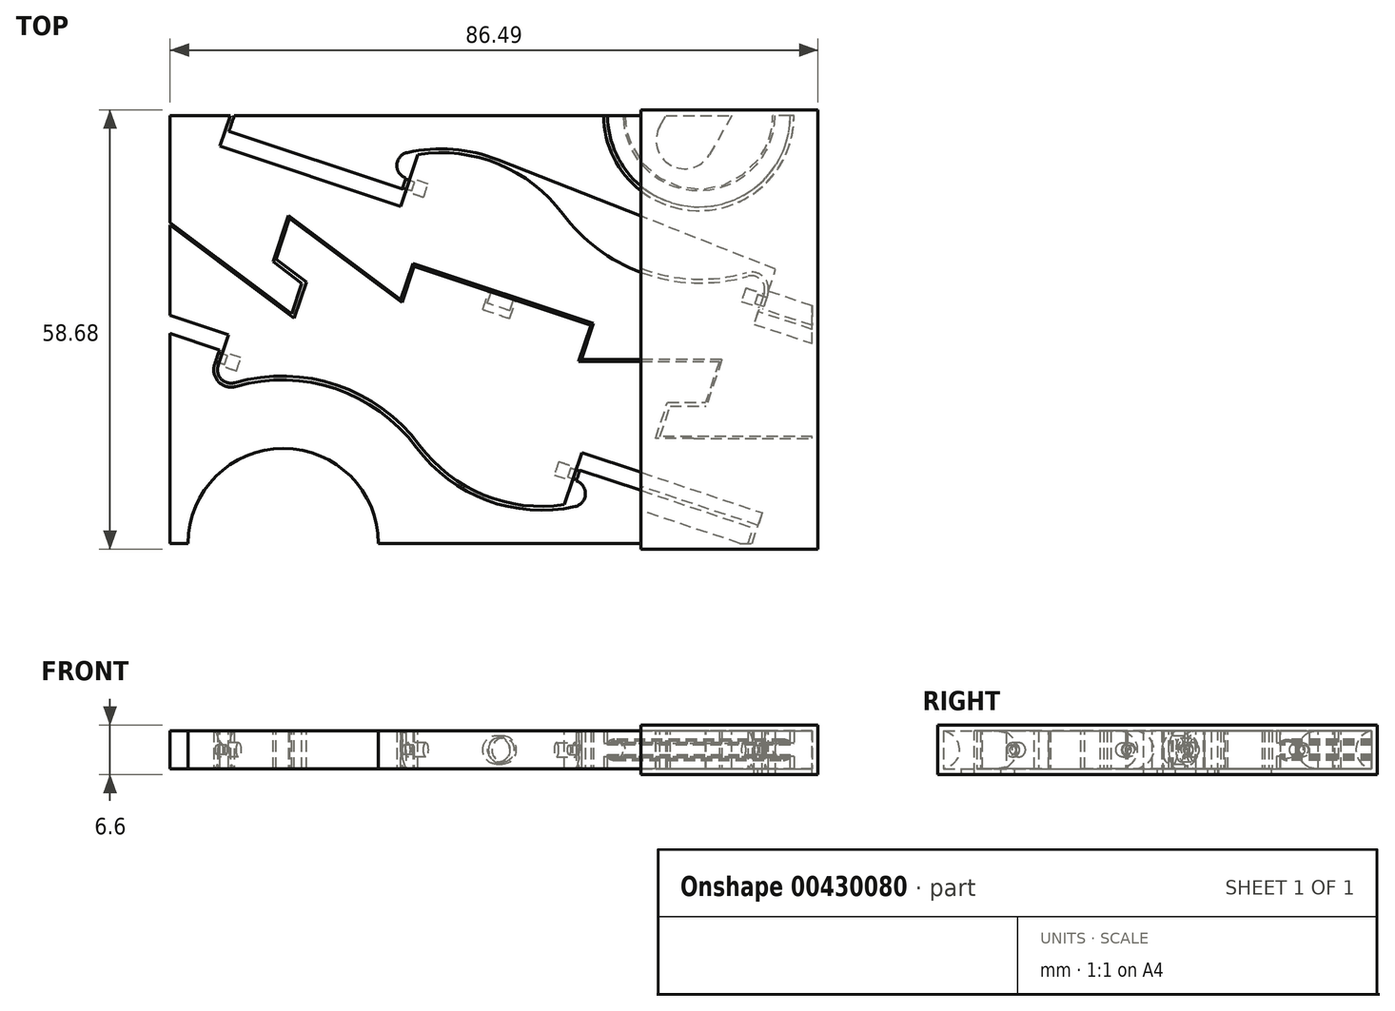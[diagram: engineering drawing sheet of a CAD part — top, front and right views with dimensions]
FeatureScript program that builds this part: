
annotation { "Feature Type Name" : "Feature", "Feature Type Description" : "" }
export const myFeature = defineFeature(function(context is Context, id is Id, definition is map)
    precondition{}
    {
        {
            var Q0;
            Q0=qCreatedBy(makeId("Top.planeOp"),FACE);
            cPlane(context, id + "F0", {"entities" : qUnion([Q0]), "cplaneType" : CPlaneType.OFFSET, "offset" : 2.54 * mm, "width" : 152.4 * mm, "height" : 152.4 * mm});
        }
        {
            var Q0;
            Q0=qCreatedBy(makeId("Top.planeOp"),FACE);
            var sketch = newSketch(context, id + "F1", { "sketchPlane" : qUnion([Q0])});
            skLineSegment(sketch, "E0", {"start": v(0, 0) * mm, "end": v(0, 28.58) * mm});
            skLineSegment(sketch, "E1", {"start": v(0, 0) * mm, "end": v(85.73, 0) * mm, "construction": true});
            skLineSegment(sketch, "E2", {"start": v(0, 28.58) * mm, "end": v(85.73, 0) * mm, "construction": true});
            skLineSegment(sketch, "E3", {"start": v(0, 28.58) * mm, "end": v(8.03, 28.58) * mm});
            skLineSegment(sketch, "E4", {"start": v(8.03, 28.58) * mm, "end": v(7.23, 26.17) * mm});
            skLineSegment(sketch, "E5", {"start": v(7.23, 26.17) * mm, "end": v(31.33, 18.13) * mm});
            skLineSegment(sketch, "E6", {"start": v(31.33, 18.13) * mm, "end": v(32.13, 20.54) * mm});
            skLineSegment(sketch, "E7", {"start": v(32.13, 20.54) * mm, "end": v(31.65, 20.7) * mm});
            skArc(sketch, "E8", {"start": v(31.78, 23.15) * mm, "mid": v(30.78, 21.98) * mm, "end": v(31.65, 20.7) * mm});
            skArc(sketch, "E9", {"start": v(52.44, 15.43) * mm, "mid": v(43.25, 22.34) * mm, "end": v(31.78, 23.15) * mm});
            skArc(sketch, "E10", {"start": v(52.44, 15.43) * mm, "mid": v(63.47, 7.42) * mm, "end": v(77.1, 7.11) * mm});
            skArc(sketch, "E11", {"start": v(79.3, 4.82) * mm, "mid": v(78.9, 6.63) * mm, "end": v(77.1, 7.11) * mm});
            skLineSegment(sketch, "E12", {"start": v(79.3, 4.82) * mm, "end": v(78.5, 2.4) * mm});
            skLineSegment(sketch, "E13", {"start": v(78.5, 2.4) * mm, "end": v(85.73, 0) * mm});
            skLineSegment(sketch, "E14", {"start": v(0, 0) * mm, "end": v(0, -28.58) * mm, "construction": true});
            skLineSegment(sketch, "E15", {"start": v(0, -28.58) * mm, "end": v(85.73, -28.58) * mm, "construction": true});
            skLineSegment(sketch, "E16", {"start": v(0, 14.29) * mm, "end": v(85.73, -14.29) * mm, "construction": true});
            skLineSegment(sketch, "E17", {"start": v(85.73, 0) * mm, "end": v(85.73, -14.29) * mm});
            skLineSegment(sketch, "E18", {"start": v(85.73, -14.29) * mm, "end": v(70.23, -14.29) * mm});
            skLineSegment(sketch, "E19", {"start": v(73.65, -4.02) * mm, "end": v(54.91, -4.02) * mm});
            skLineSegment(sketch, "E20", {"start": v(54.91, -4.02) * mm, "end": v(56.52, 0.8) * mm});
            skLineSegment(sketch, "E21", {"start": v(56.52, 0.8) * mm, "end": v(32.42, 8.84) * mm});
            skLineSegment(sketch, "E22", {"start": v(32.42, 8.84) * mm, "end": v(30.81, 4.02) * mm});
            skLineSegment(sketch, "E23", {"start": v(30.81, 4.02) * mm, "end": v(15.82, 15.26) * mm});
            skLineSegment(sketch, "E24", {"start": v(12.4, 5) * mm, "end": v(0, 14.29) * mm});
            skLineSegment(sketch, "E25", {"start": v(15.82, 15.26) * mm, "end": v(12.4, 5) * mm});
            skLineSegment(sketch, "E26", {"start": v(73.65, -4.02) * mm, "end": v(70.23, -14.29) * mm});
            skSolve(sketch);
        }
        {
            var Q0;
            Q0=qCreatedBy(makeId("Top.planeOp"),FACE);
            var sketch = newSketch(context, id + "F2", { "sketchPlane" : qUnion([Q0])});
            skLineSegment(sketch, "E27", {"start": v(85.73, 0) * mm, "end": v(85.73, -28.58) * mm, "construction": true});
            skLineSegment(sketch, "E28", {"start": v(85.73, 0) * mm, "end": v(0, 0) * mm, "construction": true});
            skLineSegment(sketch, "E29", {"start": v(85.73, -28.58) * mm, "end": v(0, 0) * mm, "construction": true});
            skLineSegment(sketch, "E30", {"start": v(85.73, -28.58) * mm, "end": v(77.7, -28.58) * mm});
            skLineSegment(sketch, "E31", {"start": v(77.7, -28.58) * mm, "end": v(78.5, -26.17) * mm});
            skLineSegment(sketch, "E32", {"start": v(78.5, -26.17) * mm, "end": v(54.4, -18.13) * mm});
            skLineSegment(sketch, "E33", {"start": v(54.4, -18.13) * mm, "end": v(53.6, -20.54) * mm});
            skLineSegment(sketch, "E34", {"start": v(53.6, -20.54) * mm, "end": v(54.08, -20.7) * mm});
            skArc(sketch, "E35", {"start": v(53.95, -23.15) * mm, "mid": v(54.94, -21.98) * mm, "end": v(54.08, -20.7) * mm});
            skArc(sketch, "E36", {"start": v(33.29, -15.43) * mm, "mid": v(42.48, -22.34) * mm, "end": v(53.95, -23.15) * mm});
            skArc(sketch, "E37", {"start": v(33.29, -15.43) * mm, "mid": v(22.26, -7.42) * mm, "end": v(8.62, -7.11) * mm});
            skArc(sketch, "E38", {"start": v(6.43, -4.82) * mm, "mid": v(6.83, -6.63) * mm, "end": v(8.62, -7.11) * mm});
            skLineSegment(sketch, "E39", {"start": v(6.43, -4.82) * mm, "end": v(7.23, -2.4) * mm});
            skLineSegment(sketch, "E40", {"start": v(7.23, -2.4) * mm, "end": v(0, 0) * mm});
            skLineSegment(sketch, "E41", {"start": v(85.73, 0) * mm, "end": v(85.73, 28.58) * mm, "construction": true});
            skLineSegment(sketch, "E42", {"start": v(85.73, 28.58) * mm, "end": v(0, 28.58) * mm, "construction": true});
            skLineSegment(sketch, "E43", {"start": v(85.73, -14.29) * mm, "end": v(0, 14.29) * mm, "construction": true});
            skLineSegment(sketch, "E44", {"start": v(0, 0) * mm, "end": v(0, 14.29) * mm, "construction": true});
            skLineSegment(sketch, "E45", {"start": v(0, 0) * mm, "end": v(0, 13.97) * mm});
            skLineSegment(sketch, "E46", {"start": v(12.53, 4.58) * mm, "end": v(15.95, 14.85) * mm});
            skLineSegment(sketch, "E47", {"start": v(15.95, 14.85) * mm, "end": v(30.94, 3.6) * mm});
            skLineSegment(sketch, "E48", {"start": v(30.94, 3.6) * mm, "end": v(32.55, 8.42) * mm});
            skLineSegment(sketch, "E49", {"start": v(32.55, 8.42) * mm, "end": v(56.16, 0.55) * mm});
            skLineSegment(sketch, "E50", {"start": v(56.16, 0.55) * mm, "end": v(54.56, -4.27) * mm});
            skLineSegment(sketch, "E51", {"start": v(54.56, -4.27) * mm, "end": v(73.3, -4.27) * mm});
            skLineSegment(sketch, "E52", {"start": v(73.3, -4.27) * mm, "end": v(69.88, -14.54) * mm});
            skLineSegment(sketch, "E53", {"start": v(69.88, -14.54) * mm, "end": v(85.73, -14.54) * mm});
            skLineSegment(sketch, "E54", {"start": v(0, 13.97) * mm, "end": v(12.53, 4.58) * mm});
            skLineSegment(sketch, "E55", {"start": v(6.26, 9.27) * mm, "end": v(6.42, 9.48) * mm, "construction": true});
            skLineSegment(sketch, "E56", {"start": v(14.24, 9.71) * mm, "end": v(14, 9.8) * mm, "construction": true});
            skLineSegment(sketch, "E57", {"start": v(71.59, -9.4) * mm, "end": v(71.83, -9.49) * mm, "construction": true});
            skLineSegment(sketch, "E58", {"start": v(77.8, -14.54) * mm, "end": v(77.8, -14.29) * mm, "construction": true});
            skLineSegment(sketch, "E59", {"start": v(85.73, -14.54) * mm, "end": v(85.73, -28.58) * mm});
            skSolve(sketch);
        }
        {
            var Q0;
            Q0=qCreatedBy(makeId("Top.planeOp"),FACE);
            var sketch = newSketch(context, id + "F3", { "sketchPlane" : qUnion([Q0])});
            skLineSegment(sketch, "E60.0", {"start": v(79.14, 2.73) * mm, "end": v(85.73, 0.54) * mm});
            skLineSegment(sketch, "E60.1", {"start": v(79.78, 4.66) * mm, "end": v(79.14, 2.73) * mm});
            skArc(sketch, "E60.2", {"start": v(79.78, 4.66) * mm, "mid": v(79.26, 6.98) * mm, "end": v(76.96, 7.6) * mm});
            skArc(sketch, "E60.3", {"start": v(52.85, 15.74) * mm, "mid": v(63.63, 7.9) * mm, "end": v(76.96, 7.6) * mm});
            skArc(sketch, "E60.4", {"start": v(52.85, 15.74) * mm, "mid": v(43.42, 22.81) * mm, "end": v(31.67, 23.64) * mm});
            skLineSegment(sketch, "E60.5", {"start": v(8.57, 28.58) * mm, "end": v(7.87, 26.49) * mm});
            skLineSegment(sketch, "E60.6", {"start": v(7.87, 26.49) * mm, "end": v(31, 18.78) * mm});
            skLineSegment(sketch, "E60.7", {"start": v(31, 18.78) * mm, "end": v(31.49, 20.22) * mm});
            skArc(sketch, "E60.8", {"start": v(31.67, 23.64) * mm, "mid": v(30.27, 22) * mm, "end": v(31.49, 20.22) * mm});
            skLineSegment(sketch, "E61", {"start": v(8.57, 28.58) * mm, "end": v(57.91, 28.58) * mm});
            skLineSegment(sketch, "E62", {"start": v(85.73, 28.58) * mm, "end": v(85.73, 0.54) * mm});
            skLineSegment(sketch, "E63", {"start": v(85.73, 28.58) * mm, "end": v(83.31, 28.58) * mm});
            skArc(sketch, "E64", {"start": v(57.91, 28.58) * mm, "mid": v(70.61, 15.88) * mm, "end": v(83.31, 28.58) * mm});
            skLineSegment(sketch, "E65", {"start": v(70.78, 29.08) * mm, "end": v(63.55, 7.4) * mm, "construction": true});
            skPoint(sketch, "E66", {"position": v(42.86, 0) * mm});
            skArc(sketch, "E67.1.0", {"start": v(54.06, -23.64) * mm, "mid": v(55.45, -22) * mm, "end": v(54.24, -20.22) * mm});
            skLineSegment(sketch, "E67.1.1", {"start": v(77.85, -26.49) * mm, "end": v(54.72, -18.78) * mm});
            skLineSegment(sketch, "E67.1.2", {"start": v(77.16, -28.58) * mm, "end": v(27.81, -28.58) * mm});
            skArc(sketch, "E67.1.3", {"start": v(32.88, -15.74) * mm, "mid": v(42.3, -22.81) * mm, "end": v(54.06, -23.64) * mm});
            skArc(sketch, "E67.1.4", {"start": v(32.88, -15.74) * mm, "mid": v(22.1, -7.9) * mm, "end": v(8.76, -7.6) * mm});
            skLineSegment(sketch, "E67.1.5", {"start": v(6.59, -2.73) * mm, "end": v(0, -0.54) * mm});
            skArc(sketch, "E67.1.6", {"start": v(27.81, -28.58) * mm, "mid": v(15.11, -15.88) * mm, "end": v(2.41, -28.58) * mm});
            skLineSegment(sketch, "E67.1.7", {"start": v(14.95, -29.08) * mm, "end": v(22.18, -7.4) * mm, "construction": true});
            skArc(sketch, "E67.1.8", {"start": v(5.94, -4.66) * mm, "mid": v(6.47, -6.98) * mm, "end": v(8.76, -7.6) * mm});
            skLineSegment(sketch, "E67.1.9", {"start": v(0, -28.58) * mm, "end": v(0, -0.54) * mm});
            skLineSegment(sketch, "E67.1.10", {"start": v(77.16, -28.58) * mm, "end": v(77.85, -26.49) * mm});
            skLineSegment(sketch, "E67.1.11", {"start": v(54.72, -18.78) * mm, "end": v(54.24, -20.22) * mm});
            skLineSegment(sketch, "E67.1.12", {"start": v(0, -28.58) * mm, "end": v(2.41, -28.58) * mm});
            skLineSegment(sketch, "E67.1.13", {"start": v(5.94, -4.66) * mm, "end": v(6.59, -2.73) * mm});
            skSolve(sketch);
        }
        {
            var Q0;
            Q0 = qSketchRegion(id + "F1", true);
            extrude(context, id + "F4", {"entities" : qUnion([Q0]), "depth" : 5.08 * mm});
        }
        {
            var Q0;
            Q0 = qSketchRegion(id + "F2", true);
            extrude(context, id + "F5", {"entities" : qUnion([Q0]), "depth" : 5.08 * mm});
        }
        {
            var Q0;
            Q0 = qSketchRegion(id + "F3", true);
            extrude(context, id + "F6", {"entities" : qUnion([Q0]), "depth" : 5.08 * mm});
        }
        {
            var Q0;
            Q0=makeQuery(id+"F4.opExtrude","SWEPT_FACE",FACE,{"disambiguationData":[OSD([sQuery(id+"F1.wireOp",EDGE,"E6")])]});
            var sketch = newSketch(context, id + "F7", { "sketchPlane" : qUnion([Q0])});
            skCircle(sketch, "E68", {"center": v(-28.38, 2.54) * mm, "radius": 0.95 * mm});
            skLineSegment(sketch, "E69.bottom", {"start": v(-29.65, 5.08) * mm, "end": v(-27.1, 5.08) * mm, "construction": true});
            skLineSegment(sketch, "E69.top", {"start": v(-29.65, 0) * mm, "end": v(-27.1, 0) * mm, "construction": true});
            skLineSegment(sketch, "E69.left", {"start": v(-29.65, 5.08) * mm, "end": v(-29.65, 0) * mm, "construction": true});
            skLineSegment(sketch, "E69.right", {"start": v(-27.1, 5.08) * mm, "end": v(-27.1, 0) * mm, "construction": true});
            skLineSegment(sketch, "E70", {"start": v(-29.65, 2.54) * mm, "end": v(-27.1, 2.54) * mm, "construction": true});
            skSolve(sketch);
        }
        {
            var Q0;
            Q0 = qSketchRegion(id + "F7", true);
            extrude(context, id + "F8", {"entities" : qUnion([Q0]), "operationType" : NewBodyOperationType.REMOVE, "oppositeDirection" : true, "depth" : 2.54 * mm});
        }
        {
            var Q0;
            Q0=makeQuery(id+"F6.opExtrude","SWEPT_FACE",FACE,{"disambiguationData":[OSD([sQuery(id+"F3.wireOp",EDGE,"E60.7")])]});
            var sketch = newSketch(context, id + "F9", { "sketchPlane" : qUnion([Q0])});
            skLineSegment(sketch, "E71", {"start": v(29.14, 5.08) * mm, "end": v(29.14, 0) * mm, "construction": true});
            skLineSegment(sketch, "E72", {"start": v(29.14, 0) * mm, "end": v(27.62, 0) * mm, "construction": true});
            skLineSegment(sketch, "E73", {"start": v(27.62, 0) * mm, "end": v(27.62, 5.08) * mm, "construction": true});
            skLineSegment(sketch, "E74", {"start": v(27.62, 5.08) * mm, "end": v(29.14, 5.08) * mm, "construction": true});
            skCircle(sketch, "E75", {"center": v(28.38, 2.54) * mm, "radius": 0.64 * mm});
            skLineSegment(sketch, "E76", {"start": v(29.14, 2.54) * mm, "end": v(27.62, 2.54) * mm, "construction": true});
            skSolve(sketch);
        }
        {
            var Q0;
            Q0 = qSketchRegion(id + "F9", true);
            extrude(context, id + "F10", {"entities" : qUnion([Q0]), "operationType" : NewBodyOperationType.ADD, "depth" : 1.27 * mm});
        }
        {
            var Q0;
            Q0=makeQuery(id+"F6.opExtrude","SWEPT_FACE",FACE,{"disambiguationData":[OSD([sQuery(id+"F3.wireOp",EDGE,"E60.1")])]});
            var sketch = newSketch(context, id + "F11", { "sketchPlane" : qUnion([Q0])});
            skLineSegment(sketch, "E77.bottom", {"start": v(-29.65, 5.08) * mm, "end": v(-27.62, 5.08) * mm, "construction": true});
            skLineSegment(sketch, "E77.top", {"start": v(-29.65, 0) * mm, "end": v(-27.62, 0) * mm, "construction": true});
            skLineSegment(sketch, "E77.left", {"start": v(-29.65, 5.08) * mm, "end": v(-29.65, 0) * mm, "construction": true});
            skLineSegment(sketch, "E77.right", {"start": v(-27.62, 5.08) * mm, "end": v(-27.62, 0) * mm, "construction": true});
            skLineSegment(sketch, "E78", {"start": v(-29.65, 2.54) * mm, "end": v(-27.62, 2.54) * mm, "construction": true});
            skCircle(sketch, "E79", {"center": v(-28.63, 2.54) * mm, "radius": 0.64 * mm});
            skSolve(sketch);
        }
        {
            var Q0;
            Q0=makeQuery(id+"F4.opExtrude","SWEPT_FACE",FACE,{"disambiguationData":[OSD([sQuery(id+"F1.wireOp",EDGE,"E12")])]});
            var sketch = newSketch(context, id + "F12", { "sketchPlane" : qUnion([Q0])});
            skLineSegment(sketch, "E80.bottom", {"start": v(29.65, 5.08) * mm, "end": v(27.62, 5.08) * mm, "construction": true});
            skLineSegment(sketch, "E80.top", {"start": v(29.65, 0) * mm, "end": v(27.62, 0) * mm, "construction": true});
            skLineSegment(sketch, "E80.left", {"start": v(29.65, 5.08) * mm, "end": v(29.65, 0) * mm, "construction": true});
            skLineSegment(sketch, "E80.right", {"start": v(27.62, 5.08) * mm, "end": v(27.62, 0) * mm, "construction": true});
            skLineSegment(sketch, "E81", {"start": v(29.65, 2.54) * mm, "end": v(27.62, 2.54) * mm, "construction": true});
            skCircle(sketch, "E82", {"center": v(28.63, 2.54) * mm, "radius": 0.95 * mm});
            skSolve(sketch);
        }
        {
            var Q0;
            Q0 = qSketchRegion(id + "F12", true);
            extrude(context, id + "F13", {"entities" : qUnion([Q0]), "operationType" : NewBodyOperationType.REMOVE, "oppositeDirection" : true, "depth" : 2.54 * mm});
        }
        {
            var Q0;
            Q0 = qSketchRegion(id + "F11", true);
            extrude(context, id + "F14", {"entities" : qUnion([Q0]), "operationType" : NewBodyOperationType.ADD, "depth" : 1.27 * mm});
        }
        {
            var Q0;
            Q0=makeQuery(id+"F4.opExtrude","SWEPT_FACE",FACE,{"disambiguationData":[OSD([sQuery(id+"F1.wireOp",EDGE,"E21")])]});
            var sketch = newSketch(context, id + "F15", { "sketchPlane" : qUnion([Q0])});
            skLineSegment(sketch, "E83.bottom", {"start": v(27.96, 5.08) * mm, "end": v(53.36, 5.08) * mm, "construction": true});
            skLineSegment(sketch, "E83.top", {"start": v(27.96, 0) * mm, "end": v(53.36, 0) * mm, "construction": true});
            skLineSegment(sketch, "E83.left", {"start": v(27.96, 5.08) * mm, "end": v(27.96, 0) * mm, "construction": true});
            skLineSegment(sketch, "E83.right", {"start": v(53.36, 5.08) * mm, "end": v(53.36, 0) * mm, "construction": true});
            skLineSegment(sketch, "E84", {"start": v(40.66, 5.08) * mm, "end": v(40.66, 0) * mm, "construction": true});
            skCircle(sketch, "E85", {"center": v(40.66, 2.54) * mm, "radius": 1.59 * mm});
            skSolve(sketch);
        }
        {
            var Q0;
            Q0=makeQuery(id+"F5.opExtrude","SWEPT_FACE",FACE,{"disambiguationData":[OSD([sQuery(id+"F2.wireOp",EDGE,"E49")])]});
            var sketch = newSketch(context, id + "F16", { "sketchPlane" : qUnion([Q0])});
            skLineSegment(sketch, "E86.bottom", {"start": v(-53.1, 5.08) * mm, "end": v(-28.22, 5.08) * mm, "construction": true});
            skLineSegment(sketch, "E86.top", {"start": v(-53.1, 0) * mm, "end": v(-28.22, 0) * mm, "construction": true});
            skLineSegment(sketch, "E86.left", {"start": v(-53.1, 5.08) * mm, "end": v(-53.1, 0) * mm, "construction": true});
            skLineSegment(sketch, "E86.right", {"start": v(-28.22, 5.08) * mm, "end": v(-28.22, 0) * mm, "construction": true});
            skLineSegment(sketch, "E87", {"start": v(-40.66, 5.08) * mm, "end": v(-40.66, 0) * mm, "construction": true});
            skCircle(sketch, "E88", {"center": v(-40.66, 2.54) * mm, "radius": 1.9 * mm});
            skSolve(sketch);
        }
        {
            var Q0;
            Q0 = qSketchRegion(id + "F16", true);
            extrude(context, id + "F17", {"entities" : qUnion([Q0]), "operationType" : NewBodyOperationType.REMOVE, "oppositeDirection" : true, "depth" : 2.54 * mm});
        }
        {
            var Q0;
            Q0 = qSketchRegion(id + "F15", true);
            extrude(context, id + "F18", {"entities" : qUnion([Q0]), "operationType" : NewBodyOperationType.ADD, "depth" : 1.9 * mm});
        }
        {
            var Q0;
            Q0=makeQuery(id+"F5.opExtrude","CAP_FACE",FACE,{"disambiguationData":[OSD([sQuery(id+"F2.wireOp",EDGE,"E30"),sQuery(id+"F2.wireOp",EDGE,"E31"),sQuery(id+"F2.wireOp",EDGE,"E32"),sQuery(id+"F2.wireOp",EDGE,"E33"),sQuery(id+"F2.wireOp",EDGE,"E34"),sQuery(id+"F2.wireOp",EDGE,"E35"),sQuery(id+"F2.wireOp",EDGE,"E36"),sQuery(id+"F2.wireOp",EDGE,"E37"),sQuery(id+"F2.wireOp",EDGE,"E38"),sQuery(id+"F2.wireOp",EDGE,"E39"),sQuery(id+"F2.wireOp",EDGE,"E40"),sQuery(id+"F2.wireOp",EDGE,"E45"),sQuery(id+"F2.wireOp",EDGE,"E46"),sQuery(id+"F2.wireOp",EDGE,"E47"),sQuery(id+"F2.wireOp",EDGE,"E48"),sQuery(id+"F2.wireOp",EDGE,"E49"),sQuery(id+"F2.wireOp",EDGE,"E50"),sQuery(id+"F2.wireOp",EDGE,"E51"),sQuery(id+"F2.wireOp",EDGE,"E52"),sQuery(id+"F2.wireOp",EDGE,"E53"),sQuery(id+"F2.wireOp",EDGE,"E54"),sQuery(id+"F2.wireOp",EDGE,"E59")])],"isStart":false});
            var sketch = newSketch(context, id + "F19", { "sketchPlane" : qUnion([Q0])});
            skLineSegment(sketch, "E89", {"start": v(12.53, 4.58) * mm, "end": v(16.6, 1.53) * mm});
            skLineSegment(sketch, "E90", {"start": v(16.6, 1.53) * mm, "end": v(18.2, 6.35) * mm});
            skLineSegment(sketch, "E91", {"start": v(18.2, 6.35) * mm, "end": v(14.13, 9.4) * mm});
            skLineSegment(sketch, "E92", {"start": v(14.13, 9.4) * mm, "end": v(12.53, 4.58) * mm});
            skLineSegment(sketch, "E93", {"start": v(44.36, 4.49) * mm, "end": v(44.64, 5.33) * mm, "construction": true});
            skLineSegment(sketch, "E94.MirrorCS", {"start": v(69.88, -14.54) * mm, "end": v(64.8, -14.54) * mm});
            skLineSegment(sketch, "E95.MirrorCS", {"start": v(64.8, -14.54) * mm, "end": v(66.4, -9.72) * mm});
            skLineSegment(sketch, "E96.MirrorCS", {"start": v(66.4, -9.72) * mm, "end": v(71.48, -9.72) * mm});
            skLineSegment(sketch, "E97.MirrorCS", {"start": v(71.48, -9.72) * mm, "end": v(69.88, -14.54) * mm});
            skSolve(sketch);
        }
        {
            var Q0;
            Q0 = qSketchRegion(id + "F19", true);
            extrude(context, id + "F20", {"entities" : qUnion([Q0]), "operationType" : NewBodyOperationType.REMOVE, "endBound" : BoundingType.THROUGH_ALL, "oppositeDirection" : true, "depth" : 25.4 * mm});
        }
        {
            var Q0;
            Q0=makeQuery(id+"F4.opExtrude","CAP_FACE",FACE,{"disambiguationData":[OSD([sQuery(id+"F1.wireOp",EDGE,"E0"),sQuery(id+"F1.wireOp",EDGE,"E3"),sQuery(id+"F1.wireOp",EDGE,"E4"),sQuery(id+"F1.wireOp",EDGE,"E5"),sQuery(id+"F1.wireOp",EDGE,"E6"),sQuery(id+"F1.wireOp",EDGE,"E7"),sQuery(id+"F1.wireOp",EDGE,"E8"),sQuery(id+"F1.wireOp",EDGE,"E9"),sQuery(id+"F1.wireOp",EDGE,"E10"),sQuery(id+"F1.wireOp",EDGE,"E11"),sQuery(id+"F1.wireOp",EDGE,"E12"),sQuery(id+"F1.wireOp",EDGE,"E13"),sQuery(id+"F1.wireOp",EDGE,"E17"),sQuery(id+"F1.wireOp",EDGE,"E18"),sQuery(id+"F1.wireOp",EDGE,"E19"),sQuery(id+"F1.wireOp",EDGE,"E20"),sQuery(id+"F1.wireOp",EDGE,"E21"),sQuery(id+"F1.wireOp",EDGE,"E22"),sQuery(id+"F1.wireOp",EDGE,"E23"),sQuery(id+"F1.wireOp",EDGE,"E24"),sQuery(id+"F1.wireOp",EDGE,"E25"),sQuery(id+"F1.wireOp",EDGE,"E26")])],"isStart":false});
            var sketch = newSketch(context, id + "F21", { "sketchPlane" : qUnion([Q0])});
            skLineSegment(sketch, "E98", {"start": v(13.75, 9.05) * mm, "end": v(17.6, 6.16) * mm});
            skLineSegment(sketch, "E99", {"start": v(17.6, 6.16) * mm, "end": v(16.25, 2.1) * mm});
            skLineSegment(sketch, "E100", {"start": v(16.25, 2.1) * mm, "end": v(12.4, 5) * mm});
            skLineSegment(sketch, "E101", {"start": v(12.4, 5) * mm, "end": v(13.75, 9.05) * mm});
            skLineSegment(sketch, "E102", {"start": v(71.58, -10.23) * mm, "end": v(66.77, -10.23) * mm});
            skLineSegment(sketch, "E103", {"start": v(66.77, -10.23) * mm, "end": v(65.42, -14.29) * mm});
            skLineSegment(sketch, "E104", {"start": v(65.42, -14.29) * mm, "end": v(70.23, -14.29) * mm});
            skLineSegment(sketch, "E105", {"start": v(70.23, -14.29) * mm, "end": v(71.58, -10.23) * mm});
            skSolve(sketch);
        }
        {
            var Q0;
            Q0 = qSketchRegion(id + "F21", true);
            var Q1;
            Q1=makeQuery(id+"F4.opExtrude","CAP_FACE",FACE,{"disambiguationData":[OSD([sQuery(id+"F1.wireOp",EDGE,"E0"),sQuery(id+"F1.wireOp",EDGE,"E3"),sQuery(id+"F1.wireOp",EDGE,"E4"),sQuery(id+"F1.wireOp",EDGE,"E5"),sQuery(id+"F1.wireOp",EDGE,"E6"),sQuery(id+"F1.wireOp",EDGE,"E7"),sQuery(id+"F1.wireOp",EDGE,"E8"),sQuery(id+"F1.wireOp",EDGE,"E9"),sQuery(id+"F1.wireOp",EDGE,"E10"),sQuery(id+"F1.wireOp",EDGE,"E11"),sQuery(id+"F1.wireOp",EDGE,"E12"),sQuery(id+"F1.wireOp",EDGE,"E13"),sQuery(id+"F1.wireOp",EDGE,"E17"),sQuery(id+"F1.wireOp",EDGE,"E18"),sQuery(id+"F1.wireOp",EDGE,"E19"),sQuery(id+"F1.wireOp",EDGE,"E20"),sQuery(id+"F1.wireOp",EDGE,"E21"),sQuery(id+"F1.wireOp",EDGE,"E22"),sQuery(id+"F1.wireOp",EDGE,"E23"),sQuery(id+"F1.wireOp",EDGE,"E24"),sQuery(id+"F1.wireOp",EDGE,"E25"),sQuery(id+"F1.wireOp",EDGE,"E26")])],"isStart":true});
            extrude(context, id + "F22", {"entities" : qUnion([Q0]), "operationType" : NewBodyOperationType.ADD, "endBound" : BoundingType.UP_TO_SURFACE, "oppositeDirection" : true, "endBoundEntityFace" : qUnion([Q1]), "depth" : 25.4 * mm});
        }
        {
            var Q0;
            Q0=makeQuery(id+"F5.opExtrude","SWEPT_FACE",FACE,{"disambiguationData":[OSD([sQuery(id+"F2.wireOp",EDGE,"E33")])]});
            var sketch = newSketch(context, id + "F23", { "sketchPlane" : qUnion([Q0])});
            skLineSegment(sketch, "E106.bottom", {"start": v(0, 5.08) * mm, "end": v(-2.54, 5.08) * mm, "construction": true});
            skLineSegment(sketch, "E106.top", {"start": v(0, 0) * mm, "end": v(-2.54, 0) * mm, "construction": true});
            skLineSegment(sketch, "E106.left", {"start": v(0, 5.08) * mm, "end": v(0, 0) * mm, "construction": true});
            skLineSegment(sketch, "E106.right", {"start": v(-2.54, 5.08) * mm, "end": v(-2.54, 0) * mm, "construction": true});
            skLineSegment(sketch, "E107", {"start": v(0, 2.54) * mm, "end": v(-2.54, 2.54) * mm, "construction": true});
            skCircle(sketch, "E108", {"center": v(-1.27, 2.54) * mm, "radius": 0.95 * mm});
            skSolve(sketch);
        }
        {
            var Q0;
            Q0=makeQuery(id+"F6.opExtrude","SWEPT_FACE",FACE,{"disambiguationData":[OSD([sQuery(id+"F3.wireOp",EDGE,"E67.1.11")])]});
            var sketch = newSketch(context, id + "F24", { "sketchPlane" : qUnion([Q0])});
            skLineSegment(sketch, "E109.bottom", {"start": v(2.03, 0) * mm, "end": v(0.5, 0) * mm, "construction": true});
            skLineSegment(sketch, "E109.top", {"start": v(2.03, 5.08) * mm, "end": v(0.5, 5.08) * mm, "construction": true});
            skLineSegment(sketch, "E109.left", {"start": v(2.03, 0) * mm, "end": v(2.03, 5.08) * mm, "construction": true});
            skLineSegment(sketch, "E109.right", {"start": v(0.5, 0) * mm, "end": v(0.5, 5.08) * mm, "construction": true});
            skLineSegment(sketch, "E110", {"start": v(0.5, 2.54) * mm, "end": v(2.03, 2.54) * mm, "construction": true});
            skCircle(sketch, "E111", {"center": v(1.27, 2.54) * mm, "radius": 0.64 * mm});
            skSolve(sketch);
        }
        {
            var Q0;
            Q0 = qSketchRegion(id + "F23", true);
            extrude(context, id + "F25", {"entities" : qUnion([Q0]), "operationType" : NewBodyOperationType.REMOVE, "oppositeDirection" : true, "depth" : 2.54 * mm});
        }
        {
            var Q0;
            Q0 = qSketchRegion(id + "F24", true);
            extrude(context, id + "F26", {"entities" : qUnion([Q0]), "operationType" : NewBodyOperationType.ADD, "depth" : 1.27 * mm});
        }
        {
            var Q0;
            Q0=makeQuery(id+"F6.opExtrude","SWEPT_FACE",FACE,{"disambiguationData":[OSD([sQuery(id+"F3.wireOp",EDGE,"E67.1.13")])]});
            var sketch = newSketch(context, id + "F27", { "sketchPlane" : qUnion([Q0])});
            skLineSegment(sketch, "E112.bottom", {"start": v(-0.5, 5.08) * mm, "end": v(-2.54, 5.08) * mm, "construction": true});
            skLineSegment(sketch, "E112.top", {"start": v(-0.5, 0) * mm, "end": v(-2.54, 0) * mm, "construction": true});
            skLineSegment(sketch, "E112.left", {"start": v(-0.5, 5.08) * mm, "end": v(-0.5, 0) * mm, "construction": true});
            skLineSegment(sketch, "E112.right", {"start": v(-2.54, 5.08) * mm, "end": v(-2.54, 0) * mm, "construction": true});
            skLineSegment(sketch, "E113", {"start": v(-0.5, 2.54) * mm, "end": v(-2.54, 2.54) * mm, "construction": true});
            skCircle(sketch, "E114", {"center": v(-1.52, 2.54) * mm, "radius": 0.64 * mm});
            skSolve(sketch);
        }
        {
            var Q0;
            Q0=makeQuery(id+"F5.opExtrude","SWEPT_FACE",FACE,{"disambiguationData":[OSD([sQuery(id+"F2.wireOp",EDGE,"E39")])]});
            var sketch = newSketch(context, id + "F28", { "sketchPlane" : qUnion([Q0])});
            skLineSegment(sketch, "E115.bottom", {"start": v(0.5, 0) * mm, "end": v(2.54, 0) * mm, "construction": true});
            skLineSegment(sketch, "E115.top", {"start": v(0.5, 5.08) * mm, "end": v(2.54, 5.08) * mm, "construction": true});
            skLineSegment(sketch, "E115.left", {"start": v(0.5, 0) * mm, "end": v(0.5, 5.08) * mm, "construction": true});
            skLineSegment(sketch, "E115.right", {"start": v(2.54, 0) * mm, "end": v(2.54, 5.08) * mm, "construction": true});
            skLineSegment(sketch, "E116", {"start": v(0.5, 2.54) * mm, "end": v(2.54, 2.54) * mm, "construction": true});
            skCircle(sketch, "E117", {"center": v(1.52, 2.54) * mm, "radius": 0.95 * mm});
            skSolve(sketch);
        }
        {
            var Q0;
            Q0 = qSketchRegion(id + "F28", true);
            extrude(context, id + "F29", {"entities" : qUnion([Q0]), "operationType" : NewBodyOperationType.REMOVE, "oppositeDirection" : true, "depth" : 2.54 * mm});
        }
        {
            var Q0;
            Q0 = qSketchRegion(id + "F27", true);
            extrude(context, id + "F30", {"entities" : qUnion([Q0]), "operationType" : NewBodyOperationType.ADD, "depth" : 1.27 * mm});
        }
        {
            var Q0;
            Q0=qCreatedBy(id+"F0.planeOp",FACE);
            var sketch = newSketch(context, id + "F31", { "sketchPlane" : qUnion([Q0])});
            skArc(sketch, "E118", {"start": v(57.91, 28.58) * mm, "mid": v(70.61, 15.88) * mm, "end": v(83.31, 28.58) * mm});
            skLineSegment(sketch, "E119", {"start": v(57.91, 28.58) * mm, "end": v(58.93, 28.58) * mm});
            skLineSegment(sketch, "E120", {"start": v(83.31, 28.58) * mm, "end": v(82.3, 28.58) * mm});
            skArc(sketch, "E121", {"start": v(58.93, 28.58) * mm, "mid": v(70.61, 16.9) * mm, "end": v(82.3, 28.58) * mm});
            skSolve(sketch);
        }
        {
            var Q0;
            Q0 = qSketchRegion(id + "F31", true);
            extrude(context, id + "F32", {"entities" : qUnion([Q0]), "operationType" : NewBodyOperationType.ADD, "depth" : 0.89 * mm, "hasSecondDirection" : true, "secondDirectionOppositeDirection" : true, "secondDirectionDepth" : 0.89 * mm});
        }
        {
            var Q0;
            Q0=makeQuery(id+"F6.opExtrude","CAP_FACE",FACE,{"disambiguationData":[OSD([sQuery(id+"F3.wireOp",EDGE,"E60.0"),sQuery(id+"F3.wireOp",EDGE,"E60.1"),sQuery(id+"F3.wireOp",EDGE,"E60.2"),sQuery(id+"F3.wireOp",EDGE,"E60.3"),sQuery(id+"F3.wireOp",EDGE,"E60.4"),sQuery(id+"F3.wireOp",EDGE,"E60.5"),sQuery(id+"F3.wireOp",EDGE,"E60.6"),sQuery(id+"F3.wireOp",EDGE,"E60.7"),sQuery(id+"F3.wireOp",EDGE,"E60.8"),sQuery(id+"F3.wireOp",EDGE,"E61"),sQuery(id+"F3.wireOp",EDGE,"E62"),sQuery(id+"F3.wireOp",EDGE,"E63"),sQuery(id+"F3.wireOp",EDGE,"E64")])],"isStart":false});
            var sketch = newSketch(context, id + "F33", { "sketchPlane" : qUnion([Q0])});
            skArc(sketch, "E122", {"start": v(58.42, 28.58) * mm, "mid": v(70.61, 16.38) * mm, "end": v(82.8, 28.58) * mm});
            skLineSegment(sketch, "E123", {"start": v(58.42, 28.58) * mm, "end": v(66.21, 28.58) * mm});
            skLineSegment(sketch, "E124", {"start": v(66.21, 28.58) * mm, "end": v(65.4, 27.18) * mm});
            skArc(sketch, "E125", {"start": v(65.4, 27.18) * mm, "mid": v(66.8, 21.98) * mm, "end": v(72, 23.37) * mm});
            skLineSegment(sketch, "E126", {"start": v(72, 23.37) * mm, "end": v(75, 28.58) * mm});
            skLineSegment(sketch, "E127", {"start": v(75, 28.58) * mm, "end": v(82.8, 28.58) * mm});
            skLineSegment(sketch, "E128", {"start": v(70.61, 28.58) * mm, "end": v(68.7, 25.28) * mm, "construction": true});
            skSolve(sketch);
        }
        {
            var Q0;
            Q0 = qSketchRegion(id + "F33", true);
            var Q1;
            Q1=makeQuery(id+"F6.opExtrude","CAP_FACE",FACE,{"disambiguationData":[OSD([sQuery(id+"F3.wireOp",EDGE,"E60.0"),sQuery(id+"F3.wireOp",EDGE,"E60.1"),sQuery(id+"F3.wireOp",EDGE,"E60.2"),sQuery(id+"F3.wireOp",EDGE,"E60.3"),sQuery(id+"F3.wireOp",EDGE,"E60.4"),sQuery(id+"F3.wireOp",EDGE,"E60.5"),sQuery(id+"F3.wireOp",EDGE,"E60.6"),sQuery(id+"F3.wireOp",EDGE,"E60.7"),sQuery(id+"F3.wireOp",EDGE,"E60.8"),sQuery(id+"F3.wireOp",EDGE,"E61"),sQuery(id+"F3.wireOp",EDGE,"E62"),sQuery(id+"F3.wireOp",EDGE,"E63"),sQuery(id+"F3.wireOp",EDGE,"E64")])],"isStart":true});
            extrude(context, id + "F34", {"entities" : qUnion([Q0]), "endBound" : BoundingType.UP_TO_SURFACE, "oppositeDirection" : true, "endBoundEntityFace" : qUnion([Q1]), "depth" : 25.4 * mm});
        }
        {
            var Q0;
            Q0=makeQuery(id+"F34.opExtrude","SWEPT_FACE",FACE,{"disambiguationData":[OSD([sQuery(id+"F33.wireOp",EDGE,"E123")])]});
            var sketch = newSketch(context, id + "F35", { "sketchPlane" : qUnion([Q0])});
            skLineSegment(sketch, "E129", {"start": v(-58.42, 2.54) * mm, "end": v(-82.8, 2.54) * mm, "construction": true});
            skLineSegment(sketch, "E130", {"start": v(-70.61, 2.54) * mm, "end": v(-70.61, 12.73) * mm, "construction": true});
            skArc(sketch, "E131", {"start": v(-58.42, 3.56) * mm, "mid": v(-60.77, 2.54) * mm, "end": v(-58.42, 1.52) * mm});
            skLineSegment(sketch, "E132", {"start": v(-58.42, 3.56) * mm, "end": v(-58.42, 1.52) * mm});
            skSolve(sketch);
        }
        {
            var Q0;
            Q0 = qSketchRegion(id + "F35", true);
            var Q1;
            Q1=sQuery(id+"F35.wireOp",EDGE,"E130");
            revolve(context, id + "F36", {"operationType" : NewBodyOperationType.REMOVE, "entities" : qUnion([Q0]), "axis" : qUnion([Q1]), "revolveType" : RevolveType.FULL, "oppositeDirection" : true});
        }
        {
            var Q0;
            Q0=makeQuery(id+"F32.boolean.opBoolean","MERGE",FACE,{"derivedFrom":[makeQuery(id+"F6.opExtrude","SWEPT_FACE",FACE,{"disambiguationData":[OSD([sQuery(id+"F3.wireOp",EDGE,"E61")])]}),makeQuery(id+"F32.opExtrude","SWEPT_FACE",FACE,{"disambiguationData":[OSD([sQuery(id+"F31.wireOp",EDGE,"E119")])]})]});
            var sketch = newSketch(context, id + "F37", { "sketchPlane" : qUnion([Q0])});
            skCircle(sketch, "E133", {"center": v(-59.38, 2.54) * mm, "radius": 1.14 * mm});
            skLineSegment(sketch, "E134", {"start": v(-57.91, 5.08) * mm, "end": v(-83.31, 5.08) * mm, "construction": true});
            skLineSegment(sketch, "E135", {"start": v(-70.61, 5.08) * mm, "end": v(-70.61, -1.36) * mm, "construction": true});
            skSolve(sketch);
        }
        {
            var Q0;
            Q0 = qSketchRegion(id + "F37", true);
            var Q1;
            Q1=sQuery(id+"F37.wireOp",EDGE,"E135");
            revolve(context, id + "F38", {"operationType" : NewBodyOperationType.ADD, "entities" : qUnion([Q0]), "axis" : qUnion([Q1]), "revolveType" : RevolveType.ONE_DIRECTION, "oppositeDirection" : true, "angle" : 180 * degree});
        }
        {
            var Q0;
            Q0=makeQuery(id+"F6.opExtrude","CAP_EDGE",EDGE,{"disambiguationData":[OSD([sQuery(id+"F3.wireOp",EDGE,"E60.0")])],"isStart":false});
            var Q1;
            Q1=makeQuery(id+"F6.opExtrude","CAP_EDGE",EDGE,{"disambiguationData":[OSD([sQuery(id+"F3.wireOp",EDGE,"E60.0")])],"isStart":true});
            var Q2;
            Q2=makeQuery(id+"F6.opExtrude","CAP_EDGE",EDGE,{"disambiguationData":[OSD([sQuery(id+"F3.wireOp",EDGE,"E60.6")])],"isStart":true});
            var Q3;
            Q3=makeQuery(id+"F6.opExtrude","CAP_EDGE",EDGE,{"disambiguationData":[OSD([sQuery(id+"F3.wireOp",EDGE,"E60.6")])],"isStart":false});
            var Q4;
            Q4=makeQuery(id+"F6.opExtrude","CAP_EDGE",EDGE,{"disambiguationData":[OSD([sQuery(id+"F3.wireOp",EDGE,"E67.1.1")])],"isStart":false});
            var Q5;
            Q5=makeQuery(id+"F6.opExtrude","CAP_EDGE",EDGE,{"disambiguationData":[OSD([sQuery(id+"F3.wireOp",EDGE,"E67.1.1")])],"isStart":true});
            var Q6;
            Q6=makeQuery(id+"F6.opExtrude","CAP_EDGE",EDGE,{"disambiguationData":[OSD([sQuery(id+"F3.wireOp",EDGE,"E67.1.5")])],"isStart":true});
            var Q7;
            Q7=makeQuery(id+"F6.opExtrude","CAP_EDGE",EDGE,{"disambiguationData":[OSD([sQuery(id+"F3.wireOp",EDGE,"E67.1.5")])],"isStart":false});
            fillet(context, id + "F39", {"entities" : qUnion([Q0, Q1, Q2, Q3, Q4, Q5, Q6, Q7]), "radius" : 2.54 * mm, "tangentPropagation" : true, "allowEdgeOverflow" : false});
        }
        {
            var Q0;
            Q0=makeQuery(id+"F6.opExtrude","SWEPT_FACE",FACE,{"disambiguationData":[OSD([sQuery(id+"F3.wireOp",EDGE,"E62")])]});
            var sketch = newSketch(context, id + "F40", { "sketchPlane" : qUnion([Q0])});
            skLineSegment(sketch, "E136.bottom", {"start": v(-29.34, 5.84) * mm, "end": v(29.34, 5.84) * mm});
            skLineSegment(sketch, "E136.top", {"start": v(-29.34, -0.76) * mm, "end": v(29.34, -0.76) * mm});
            skLineSegment(sketch, "E136.left", {"start": v(-29.34, 5.84) * mm, "end": v(-29.34, -0.76) * mm});
            skLineSegment(sketch, "E136.right", {"start": v(29.34, 5.84) * mm, "end": v(29.34, -0.76) * mm});
            skSolve(sketch);
        }
        {
            var Q0;
            Q0 = qSketchRegion(id + "F40", true);
            extrude(context, id + "F41", {"entities" : qUnion([Q0]), "depth" : 0.76 * mm});
        }
        {
            var Q0;
            Q0=makeQuery(id+"F41.opExtrude","CAP_FACE",FACE,{"disambiguationData":[OSD([sQuery(id+"F40.wireOp",EDGE,"E136.bottom"),sQuery(id+"F40.wireOp",EDGE,"E136.top"),sQuery(id+"F40.wireOp",EDGE,"E136.left"),sQuery(id+"F40.wireOp",EDGE,"E136.right")])],"isStart":true});
            var sketch = newSketch(context, id + "F42", { "sketchPlane" : qUnion([Q0])});
            skLineSegment(sketch, "E137.bottom", {"start": v(29.34, 5.84) * mm, "end": v(-29.34, 5.84) * mm});
            skLineSegment(sketch, "E137.top", {"start": v(29.34, -0.76) * mm, "end": v(-29.34, -0.76) * mm});
            skLineSegment(sketch, "E137.left", {"start": v(29.34, 5.84) * mm, "end": v(29.34, -0.76) * mm});
            skLineSegment(sketch, "E137.right", {"start": v(-29.34, 5.84) * mm, "end": v(-29.34, -0.76) * mm});
            skLineSegment(sketch, "E138.bottom", {"start": v(28.58, 5.08) * mm, "end": v(-28.58, 5.08) * mm});
            skLineSegment(sketch, "E138.top", {"start": v(28.58, 0) * mm, "end": v(-28.58, 0) * mm});
            skLineSegment(sketch, "E138.left", {"start": v(28.58, 5.08) * mm, "end": v(28.58, 0) * mm});
            skLineSegment(sketch, "E138.right", {"start": v(-28.58, 5.08) * mm, "end": v(-28.58, 0) * mm});
            skSolve(sketch);
        }
        {
            var Q0;
            Q0 = qSketchRegion(id + "F42", true);
            extrude(context, id + "F43", {"entities" : qUnion([Q0]), "operationType" : NewBodyOperationType.ADD, "depth" : 22.86 * mm});
        }
        {
            var Q0;
            Q0=makeQuery(id+"F22.boolean.opBoolean","MERGE",FACE,{"derivedFrom":[makeQuery(id+"F4.opExtrude","CAP_FACE",FACE,{"disambiguationData":[OSD([sQuery(id+"F1.wireOp",EDGE,"E0"),sQuery(id+"F1.wireOp",EDGE,"E3"),sQuery(id+"F1.wireOp",EDGE,"E4"),sQuery(id+"F1.wireOp",EDGE,"E5"),sQuery(id+"F1.wireOp",EDGE,"E6"),sQuery(id+"F1.wireOp",EDGE,"E7"),sQuery(id+"F1.wireOp",EDGE,"E8"),sQuery(id+"F1.wireOp",EDGE,"E9"),sQuery(id+"F1.wireOp",EDGE,"E10"),sQuery(id+"F1.wireOp",EDGE,"E11"),sQuery(id+"F1.wireOp",EDGE,"E12"),sQuery(id+"F1.wireOp",EDGE,"E13"),sQuery(id+"F1.wireOp",EDGE,"E17"),sQuery(id+"F1.wireOp",EDGE,"E18"),sQuery(id+"F1.wireOp",EDGE,"E19"),sQuery(id+"F1.wireOp",EDGE,"E20"),sQuery(id+"F1.wireOp",EDGE,"E21"),sQuery(id+"F1.wireOp",EDGE,"E22"),sQuery(id+"F1.wireOp",EDGE,"E23"),sQuery(id+"F1.wireOp",EDGE,"E24"),sQuery(id+"F1.wireOp",EDGE,"E25"),sQuery(id+"F1.wireOp",EDGE,"E26")])],"isStart":false}),makeQuery(id+"F22.opExtrude","CAP_FACE",FACE,{"disambiguationData":[OSD([sQuery(id+"F21.wireOp",EDGE,"E98"),sQuery(id+"F21.wireOp",EDGE,"E99"),sQuery(id+"F21.wireOp",EDGE,"E100"),sQuery(id+"F21.wireOp",EDGE,"E101")])],"isStart":true}),makeQuery(id+"F22.opExtrude","CAP_FACE",FACE,{"disambiguationData":[OSD([sQuery(id+"F21.wireOp",EDGE,"E102"),sQuery(id+"F21.wireOp",EDGE,"E103"),sQuery(id+"F21.wireOp",EDGE,"E104"),sQuery(id+"F21.wireOp",EDGE,"E105")])],"isStart":true})]});
            var sketch = newSketch(context, id + "F44", { "sketchPlane" : qUnion([Q0])});
            skLineSegment(sketch, "E139", {"start": v(32.13, 20.54) * mm, "end": v(33.08, 23.4) * mm});
            skArc(sketch, "E140", {"start": v(33.08, 23.4) * mm, "mid": v(32.42, 23.28) * mm, "end": v(31.78, 23.15) * mm});
            skLineSegment(sketch, "E141", {"start": v(32.13, 20.54) * mm, "end": v(31.65, 20.7) * mm});
            skArc(sketch, "E142", {"start": v(31.78, 23.15) * mm, "mid": v(30.78, 21.98) * mm, "end": v(31.65, 20.7) * mm});
            skSolve(sketch);
        }
        {
            var Q0;
            Q0 = qSketchRegion(id + "F44", true);
            extrude(context, id + "F45", {"entities" : qUnion([Q0]), "operationType" : NewBodyOperationType.REMOVE, "oppositeDirection" : true, "depth" : 25.4 * mm});
        }
        {
            var Q0;
            Q0=makeQuery(id+"F5.opExtrude","CAP_FACE",FACE,{"disambiguationData":[OSD([sQuery(id+"F2.wireOp",EDGE,"E30"),sQuery(id+"F2.wireOp",EDGE,"E31"),sQuery(id+"F2.wireOp",EDGE,"E32"),sQuery(id+"F2.wireOp",EDGE,"E33"),sQuery(id+"F2.wireOp",EDGE,"E34"),sQuery(id+"F2.wireOp",EDGE,"E35"),sQuery(id+"F2.wireOp",EDGE,"E36"),sQuery(id+"F2.wireOp",EDGE,"E37"),sQuery(id+"F2.wireOp",EDGE,"E38"),sQuery(id+"F2.wireOp",EDGE,"E39"),sQuery(id+"F2.wireOp",EDGE,"E40"),sQuery(id+"F2.wireOp",EDGE,"E45"),sQuery(id+"F2.wireOp",EDGE,"E46"),sQuery(id+"F2.wireOp",EDGE,"E47"),sQuery(id+"F2.wireOp",EDGE,"E48"),sQuery(id+"F2.wireOp",EDGE,"E49"),sQuery(id+"F2.wireOp",EDGE,"E50"),sQuery(id+"F2.wireOp",EDGE,"E51"),sQuery(id+"F2.wireOp",EDGE,"E52"),sQuery(id+"F2.wireOp",EDGE,"E53"),sQuery(id+"F2.wireOp",EDGE,"E54"),sQuery(id+"F2.wireOp",EDGE,"E59")])],"isStart":false});
            var sketch = newSketch(context, id + "F46", { "sketchPlane" : qUnion([Q0])});
            skLineSegment(sketch, "E143", {"start": v(53.6, -20.54) * mm, "end": v(54.08, -20.7) * mm});
            skLineSegment(sketch, "E144", {"start": v(53.6, -20.54) * mm, "end": v(52.65, -23.4) * mm});
            skArc(sketch, "E145", {"start": v(53.95, -23.15) * mm, "mid": v(54.94, -21.98) * mm, "end": v(54.08, -20.7) * mm});
            skArc(sketch, "E146", {"start": v(52.65, -23.4) * mm, "mid": v(53.3, -23.28) * mm, "end": v(53.95, -23.15) * mm});
            skSolve(sketch);
        }
        {
            var Q0;
            Q0 = qSketchRegion(id + "F46", true);
            extrude(context, id + "F47", {"entities" : qUnion([Q0]), "operationType" : NewBodyOperationType.REMOVE, "oppositeDirection" : true, "depth" : 25.4 * mm});
        }
        {
            var Q0;
            Q0=makeQuery(id+"F6.opExtrude","CAP_FACE",FACE,{"disambiguationData":[OSD([sQuery(id+"F3.wireOp",EDGE,"E60.0"),sQuery(id+"F3.wireOp",EDGE,"E60.1"),sQuery(id+"F3.wireOp",EDGE,"E60.2"),sQuery(id+"F3.wireOp",EDGE,"E60.3"),sQuery(id+"F3.wireOp",EDGE,"E60.4"),sQuery(id+"F3.wireOp",EDGE,"E60.5"),sQuery(id+"F3.wireOp",EDGE,"E60.6"),sQuery(id+"F3.wireOp",EDGE,"E60.7"),sQuery(id+"F3.wireOp",EDGE,"E60.8"),sQuery(id+"F3.wireOp",EDGE,"E61"),sQuery(id+"F3.wireOp",EDGE,"E62"),sQuery(id+"F3.wireOp",EDGE,"E63"),sQuery(id+"F3.wireOp",EDGE,"E64")])],"isStart":false});
            var sketch = newSketch(context, id + "F48", { "sketchPlane" : qUnion([Q0])});
            skLineSegment(sketch, "E147", {"start": v(79.89, 5.16) * mm, "end": v(80.85, 8.05) * mm});
            skLineSegment(sketch, "E148", {"start": v(80.85, 8.05) * mm, "end": v(43.78, 22.68) * mm});
            skArc(sketch, "E149", {"start": v(52.85, 15.74) * mm, "mid": v(48.8, 19.84) * mm, "end": v(43.78, 22.68) * mm});
            skArc(sketch, "E150", {"start": v(52.85, 15.74) * mm, "mid": v(63.63, 7.9) * mm, "end": v(76.96, 7.6) * mm});
            skArc(sketch, "E151", {"start": v(79.89, 5.16) * mm, "mid": v(79.07, 7.15) * mm, "end": v(76.96, 7.6) * mm});
            skSolve(sketch);
        }
        {
            var Q0;
            Q0 = qSketchRegion(id + "F48", true);
            extrude(context, id + "F49", {"entities" : qUnion([Q0]), "operationType" : NewBodyOperationType.REMOVE, "endBound" : BoundingType.THROUGH_ALL, "oppositeDirection" : true, "depth" : 25.4 * mm});
        }
        {
            var Q0;
            Q0=makeQuery(id+"F22.boolean.opBoolean","MERGE",FACE,{"derivedFrom":[makeQuery(id+"F4.opExtrude","CAP_FACE",FACE,{"disambiguationData":[OSD([sQuery(id+"F1.wireOp",EDGE,"E0"),sQuery(id+"F1.wireOp",EDGE,"E3"),sQuery(id+"F1.wireOp",EDGE,"E4"),sQuery(id+"F1.wireOp",EDGE,"E5"),sQuery(id+"F1.wireOp",EDGE,"E6"),sQuery(id+"F1.wireOp",EDGE,"E7"),sQuery(id+"F1.wireOp",EDGE,"E8"),sQuery(id+"F1.wireOp",EDGE,"E9"),sQuery(id+"F1.wireOp",EDGE,"E10"),sQuery(id+"F1.wireOp",EDGE,"E11"),sQuery(id+"F1.wireOp",EDGE,"E12"),sQuery(id+"F1.wireOp",EDGE,"E13"),sQuery(id+"F1.wireOp",EDGE,"E17"),sQuery(id+"F1.wireOp",EDGE,"E18"),sQuery(id+"F1.wireOp",EDGE,"E19"),sQuery(id+"F1.wireOp",EDGE,"E20"),sQuery(id+"F1.wireOp",EDGE,"E21"),sQuery(id+"F1.wireOp",EDGE,"E22"),sQuery(id+"F1.wireOp",EDGE,"E23"),sQuery(id+"F1.wireOp",EDGE,"E24"),sQuery(id+"F1.wireOp",EDGE,"E25"),sQuery(id+"F1.wireOp",EDGE,"E26")])],"isStart":false}),makeQuery(id+"F22.opExtrude","CAP_FACE",FACE,{"disambiguationData":[OSD([sQuery(id+"F21.wireOp",EDGE,"E98"),sQuery(id+"F21.wireOp",EDGE,"E99"),sQuery(id+"F21.wireOp",EDGE,"E100"),sQuery(id+"F21.wireOp",EDGE,"E101")])],"isStart":true}),makeQuery(id+"F22.opExtrude","CAP_FACE",FACE,{"disambiguationData":[OSD([sQuery(id+"F21.wireOp",EDGE,"E102"),sQuery(id+"F21.wireOp",EDGE,"E103"),sQuery(id+"F21.wireOp",EDGE,"E104"),sQuery(id+"F21.wireOp",EDGE,"E105")])],"isStart":true})]});
            var sketch = newSketch(context, id + "F50", { "sketchPlane" : qUnion([Q0])});
            skLineSegment(sketch, "E152", {"start": v(7.23, 26.17) * mm, "end": v(6.67, 24.48) * mm});
            skLineSegment(sketch, "E153", {"start": v(6.67, 24.48) * mm, "end": v(30.76, 16.45) * mm});
            skLineSegment(sketch, "E154", {"start": v(30.76, 16.45) * mm, "end": v(31.33, 18.13) * mm});
            skLineSegment(sketch, "E155", {"start": v(31.33, 18.13) * mm, "end": v(7.23, 26.17) * mm});
            skLineSegment(sketch, "E156", {"start": v(77.93, 0.72) * mm, "end": v(85.73, -1.87) * mm});
            skLineSegment(sketch, "E157", {"start": v(85.73, -1.87) * mm, "end": v(85.73, 0) * mm});
            skLineSegment(sketch, "E158", {"start": v(85.73, 0) * mm, "end": v(78.5, 2.4) * mm});
            skLineSegment(sketch, "E159", {"start": v(78.5, 2.4) * mm, "end": v(77.93, 0.72) * mm});
            skSolve(sketch);
        }
        {
            var Q0;
            Q0 = qSketchRegion(id + "F50", true);
            extrude(context, id + "F51", {"entities" : qUnion([Q0]), "operationType" : NewBodyOperationType.REMOVE, "endBound" : BoundingType.THROUGH_ALL, "oppositeDirection" : true, "depth" : 25.4 * mm});
        }
        {
            var Q0;
            Q0=makeQuery(id+"F5.opExtrude","CAP_FACE",FACE,{"disambiguationData":[OSD([sQuery(id+"F2.wireOp",EDGE,"E30"),sQuery(id+"F2.wireOp",EDGE,"E31"),sQuery(id+"F2.wireOp",EDGE,"E32"),sQuery(id+"F2.wireOp",EDGE,"E33"),sQuery(id+"F2.wireOp",EDGE,"E34"),sQuery(id+"F2.wireOp",EDGE,"E35"),sQuery(id+"F2.wireOp",EDGE,"E36"),sQuery(id+"F2.wireOp",EDGE,"E37"),sQuery(id+"F2.wireOp",EDGE,"E38"),sQuery(id+"F2.wireOp",EDGE,"E39"),sQuery(id+"F2.wireOp",EDGE,"E40"),sQuery(id+"F2.wireOp",EDGE,"E45"),sQuery(id+"F2.wireOp",EDGE,"E46"),sQuery(id+"F2.wireOp",EDGE,"E47"),sQuery(id+"F2.wireOp",EDGE,"E48"),sQuery(id+"F2.wireOp",EDGE,"E49"),sQuery(id+"F2.wireOp",EDGE,"E50"),sQuery(id+"F2.wireOp",EDGE,"E51"),sQuery(id+"F2.wireOp",EDGE,"E52"),sQuery(id+"F2.wireOp",EDGE,"E53"),sQuery(id+"F2.wireOp",EDGE,"E54"),sQuery(id+"F2.wireOp",EDGE,"E59")])],"isStart":false});
            var sketch = newSketch(context, id + "F52", { "sketchPlane" : qUnion([Q0])});
            skLineSegment(sketch, "E160", {"start": v(0, 0) * mm, "end": v(0, 1.87) * mm});
            skLineSegment(sketch, "E161", {"start": v(0, 1.87) * mm, "end": v(7.8, -0.72) * mm});
            skLineSegment(sketch, "E162", {"start": v(7.8, -0.72) * mm, "end": v(7.23, -2.4) * mm});
            skLineSegment(sketch, "E163", {"start": v(7.23, -2.4) * mm, "end": v(0, 0) * mm});
            skLineSegment(sketch, "E164", {"start": v(54.4, -18.13) * mm, "end": v(54.96, -16.45) * mm});
            skLineSegment(sketch, "E165", {"start": v(54.96, -16.45) * mm, "end": v(79.06, -24.48) * mm});
            skLineSegment(sketch, "E166", {"start": v(79.06, -24.48) * mm, "end": v(78.5, -26.17) * mm});
            skLineSegment(sketch, "E167", {"start": v(78.5, -26.17) * mm, "end": v(54.4, -18.13) * mm});
            skSolve(sketch);
        }
        {
            var Q0;
            Q0 = qSketchRegion(id + "F52", true);
            extrude(context, id + "F53", {"entities" : qUnion([Q0]), "operationType" : NewBodyOperationType.REMOVE, "endBound" : BoundingType.THROUGH_ALL, "oppositeDirection" : true, "depth" : 25.4 * mm});
        }
    });
